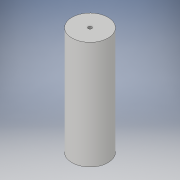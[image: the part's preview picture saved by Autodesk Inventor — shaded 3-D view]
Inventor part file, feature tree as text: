
AUTODESK INVENTOR PART (.ipt)
format: ipt  version: 2019 (Build 230136000, 136)  size: 97,280 bytes
history: native  units: mm
features: other x1, extrude x1, sketch x1
ambient origin geometry x8: Origin, YZ Plane, XZ Plane, XY Plane, X Axis, Y Axis, Z Axis, Center Point
bodies: Body1 (feature_tree)
feature tree (3):
  other  "ソリッド1"
  extrude  "押し出し1"  Depth=2.0mm
  sketch  "スケッチ1"
